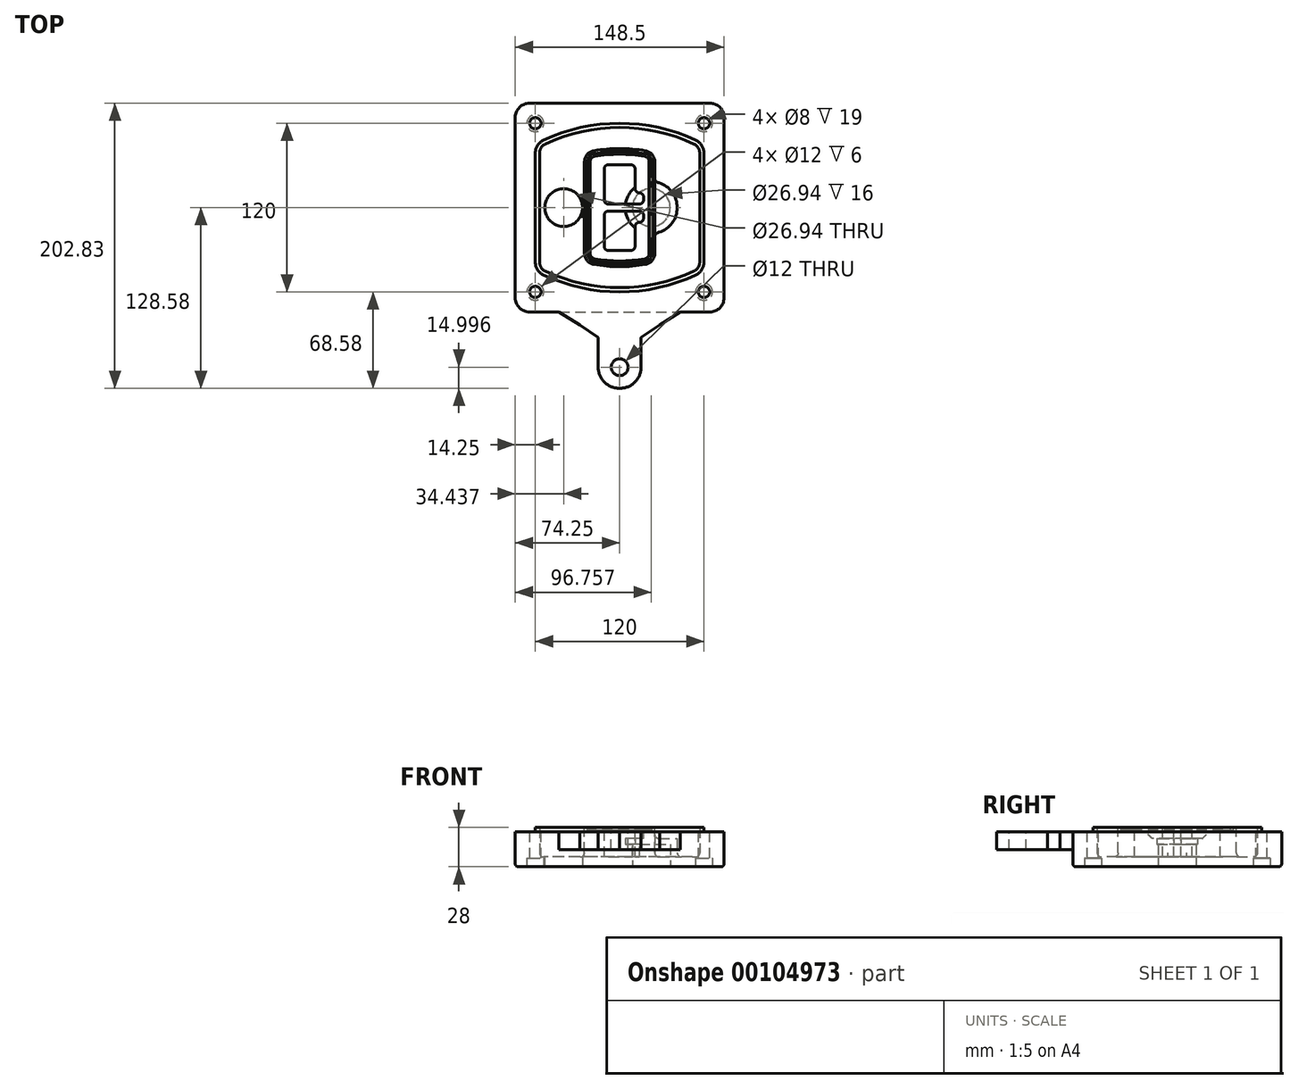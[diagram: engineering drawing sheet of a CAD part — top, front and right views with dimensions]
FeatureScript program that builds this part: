
annotation { "Feature Type Name" : "Feature", "Feature Type Description" : "" }
export const myFeature = defineFeature(function(context is Context, id is Id, definition is map)
    precondition{}
    {
        {
            var Q0;
            Q0=qCreatedBy(makeId("Top.planeOp"),FACE);
            var sketch = newSketch(context, id + "F0", { "sketchPlane" : qUnion([Q0])});
            skPoint(sketch, "E0.rect.middle", {"position": v(0, 0) * mm});
            skLineSegment(sketch, "E1.bottom", {"start": v(-64.25, -74.25) * mm, "end": v(64.25, -74.25) * mm});
            skLineSegment(sketch, "E1.top", {"start": v(-64.25, 74.25) * mm, "end": v(64.25, 74.25) * mm});
            skLineSegment(sketch, "E1.left", {"start": v(-74.25, -64.25) * mm, "end": v(-74.25, 64.25) * mm});
            skLineSegment(sketch, "E1.right", {"start": v(74.25, -64.25) * mm, "end": v(74.25, 64.25) * mm});
            skLineSegment(sketch, "E2", {"start": v(-74.25, 74.25) * mm, "end": v(74.25, -74.25) * mm, "construction": true});
            skLineSegment(sketch, "E3", {"start": v(74.25, 74.25) * mm, "end": v(-74.25, -74.25) * mm, "construction": true});
            skCircle(sketch, "E4", {"center": v(-60, 60) * mm, "radius": 4 * mm});
            skCircle(sketch, "E5", {"center": v(60, 60) * mm, "radius": 4 * mm});
            skCircle(sketch, "E6", {"center": v(60, -60) * mm, "radius": 4 * mm});
            skCircle(sketch, "E7", {"center": v(-60, -60) * mm, "radius": 4 * mm});
            skLineSegment(sketch, "E8", {"start": v(-60, 60) * mm, "end": v(60, 60) * mm, "construction": true});
            skLineSegment(sketch, "E9", {"start": v(60, 60) * mm, "end": v(60, -60) * mm, "construction": true});
            skLineSegment(sketch, "E10", {"start": v(60, -60) * mm, "end": v(-60, -60) * mm, "construction": true});
            skLineSegment(sketch, "E11", {"start": v(-60, -60) * mm, "end": v(-60, 60) * mm, "construction": true});
            skLineSegment(sketch, "E12", {"start": v(-60, 38.83) * mm, "end": v(-60, -38.83) * mm});
            skLineSegment(sketch, "E13", {"start": v(60, 38.83) * mm, "end": v(60, -38.83) * mm});
            skArc(sketch, "E14", {"start": v(54.26, 47.88) * mm, "mid": v(0, 60) * mm, "end": v(-54.26, 47.88) * mm});
            skArc(sketch, "E15", {"start": v(-54.26, -47.88) * mm, "mid": v(0, -60) * mm, "end": v(54.26, -47.88) * mm});
            skLineSegment(sketch, "E16", {"start": v(-60, 0) * mm, "end": v(60, 0) * mm, "construction": true});
            skPoint(sketch, "E17.visualSharp", {"position": v(-60, -45) * mm});
            skArc(sketch, "E17.filletArc", {"start": v(-60, -38.83) * mm, "mid": v(-58.44, -44.2) * mm, "end": v(-54.26, -47.88) * mm});
            skPoint(sketch, "E18.visualSharp", {"position": v(-60, 45) * mm});
            skArc(sketch, "E18.filletArc", {"start": v(-54.26, 47.88) * mm, "mid": v(-58.44, 44.2) * mm, "end": v(-60, 38.83) * mm});
            skPoint(sketch, "E19.visualSharp", {"position": v(60, 45) * mm});
            skArc(sketch, "E19.filletArc", {"start": v(60, 38.83) * mm, "mid": v(58.44, 44.2) * mm, "end": v(54.26, 47.88) * mm});
            skPoint(sketch, "E20.visualSharp", {"position": v(60, -45) * mm});
            skArc(sketch, "E20.filletArc", {"start": v(54.26, -47.88) * mm, "mid": v(58.44, -44.2) * mm, "end": v(60, -38.83) * mm});
            skPoint(sketch, "E21.visualSharp", {"position": v(-74.25, 74.25) * mm});
            skArc(sketch, "E21.filletArc", {"start": v(-64.25, 74.25) * mm, "mid": v(-71.32, 71.32) * mm, "end": v(-74.25, 64.25) * mm});
            skPoint(sketch, "E22.visualSharp", {"position": v(74.25, 74.25) * mm});
            skArc(sketch, "E22.filletArc", {"start": v(74.25, 64.25) * mm, "mid": v(71.32, 71.32) * mm, "end": v(64.25, 74.25) * mm});
            skPoint(sketch, "E23.visualSharp", {"position": v(74.25, -74.25) * mm});
            skArc(sketch, "E23.filletArc", {"start": v(64.25, -74.25) * mm, "mid": v(71.32, -71.32) * mm, "end": v(74.25, -64.25) * mm});
            skPoint(sketch, "E24.visualSharp", {"position": v(-74.25, -74.25) * mm});
            skArc(sketch, "E24.filletArc", {"start": v(-74.25, -64.25) * mm, "mid": v(-71.32, -71.32) * mm, "end": v(-64.25, -74.25) * mm});
            skArc(sketch, "E25.0", {"start": v(57, 38.83) * mm, "mid": v(55.9, 42.58) * mm, "end": v(52.98, 45.17) * mm});
            skLineSegment(sketch, "E25.1", {"start": v(57, 38.83) * mm, "end": v(57, -38.83) * mm});
            skArc(sketch, "E25.2", {"start": v(52.98, -45.17) * mm, "mid": v(55.9, -42.58) * mm, "end": v(57, -38.83) * mm});
            skArc(sketch, "E25.3", {"start": v(-52.98, -45.17) * mm, "mid": v(0, -57) * mm, "end": v(52.98, -45.17) * mm});
            skArc(sketch, "E25.4", {"start": v(-57, -38.83) * mm, "mid": v(-55.9, -42.58) * mm, "end": v(-52.98, -45.17) * mm});
            skArc(sketch, "E25.5", {"start": v(52.98, 45.17) * mm, "mid": v(0, 57) * mm, "end": v(-52.98, 45.17) * mm});
            skLineSegment(sketch, "E25.6", {"start": v(-57, 38.83) * mm, "end": v(-57, -38.83) * mm});
            skArc(sketch, "E25.7", {"start": v(-52.98, 45.17) * mm, "mid": v(-55.9, 42.58) * mm, "end": v(-57, 38.83) * mm});
            skArc(sketch, "E26.0", {"start": v(-55.96, 51.5) * mm, "mid": v(-61.82, 46.33) * mm, "end": v(-64, 38.83) * mm});
            skArc(sketch, "E26.1", {"start": v(55.96, 51.5) * mm, "mid": v(0, 64) * mm, "end": v(-55.96, 51.5) * mm});
            skArc(sketch, "E26.2", {"start": v(64, 38.83) * mm, "mid": v(61.82, 46.33) * mm, "end": v(55.96, 51.5) * mm});
            skLineSegment(sketch, "E26.3", {"start": v(64, 38.83) * mm, "end": v(64, -38.83) * mm});
            skArc(sketch, "E26.4", {"start": v(55.96, -51.5) * mm, "mid": v(61.82, -46.33) * mm, "end": v(64, -38.83) * mm});
            skLineSegment(sketch, "E26.5", {"start": v(-64, 38.83) * mm, "end": v(-64, -38.83) * mm});
            skArc(sketch, "E26.6", {"start": v(-55.96, -51.5) * mm, "mid": v(0, -64) * mm, "end": v(55.96, -51.5) * mm});
            skArc(sketch, "E26.7", {"start": v(-64, -38.83) * mm, "mid": v(-61.82, -46.33) * mm, "end": v(-55.96, -51.5) * mm});
            skSolve(sketch);
        }
        {
            var Q0;
            Q0=makeQuery(id+"F0.imprint","IMPRINT",FACE,{"disambiguationData":[TD([[makeQuery(id+"F0.imprint","IMPRINT",EDGE,{"derivedFrom":sQuery(id+"F0.wireOp",EDGE,"E1.bottom")}),1.0]])]});
            var Q1;
            Q1=makeQuery(id+"F0.imprint","IMPRINT",FACE,{"disambiguationData":[TD([[makeQuery(id+"F0.imprint","IMPRINT",EDGE,{"derivedFrom":sQuery(id+"F0.wireOp",EDGE,"E12")}),1.0]])]});
            var Q2;
            Q2=makeQuery(id+"F0.imprint","IMPRINT",FACE,{"disambiguationData":[TD([[makeQuery(id+"F0.imprint","IMPRINT",EDGE,{"derivedFrom":sQuery(id+"F0.wireOp",EDGE,"E25.0")}),1.0]])]});
            var Q3;
            Q3=makeQuery(id+"F0.imprint","IMPRINT",FACE,{"disambiguationData":[TD([[makeQuery(id+"F0.imprint","IMPRINT",EDGE,{"derivedFrom":sQuery(id+"F0.wireOp",EDGE,"E12")}),-1.0]])]});
            extrude(context, id + "F1", {"entities" : qUnion([Q0, Q1, Q2, Q3]), "oppositeDirection" : true, "depth" : 25 * mm});
        }
        {
            var Q0;
            Q0=makeQuery(id+"F0.imprint","IMPRINT",FACE,{"disambiguationData":[TD([[makeQuery(id+"F0.imprint","IMPRINT",EDGE,{"derivedFrom":sQuery(id+"F0.wireOp",EDGE,"E12")}),1.0]])]});
            extrude(context, id + "F2", {"entities" : qUnion([Q0]), "operationType" : NewBodyOperationType.ADD, "depth" : 3 * mm});
        }
        {
            var Q0;
            Q0=makeQuery(id+"F0.imprint","IMPRINT",FACE,{"disambiguationData":[TD([[makeQuery(id+"F0.imprint","IMPRINT",EDGE,{"derivedFrom":sQuery(id+"F0.wireOp",EDGE,"E25.0")}),1.0]])]});
            extrude(context, id + "F3", {"entities" : qUnion([Q0]), "operationType" : NewBodyOperationType.REMOVE, "oppositeDirection" : true, "depth" : 18 * mm});
        }
        {
            var Q0;
            Q0=makeQuery(id+"F2.opExtrude","CAP_FACE",FACE,{"disambiguationData":[OSD([sQuery(id+"F0.wireOp",EDGE,"E12"),sQuery(id+"F0.wireOp",EDGE,"E13"),sQuery(id+"F0.wireOp",EDGE,"E14"),sQuery(id+"F0.wireOp",EDGE,"E15"),sQuery(id+"F0.wireOp",EDGE,"E17.filletArc"),sQuery(id+"F0.wireOp",EDGE,"E18.filletArc"),sQuery(id+"F0.wireOp",EDGE,"E19.filletArc"),sQuery(id+"F0.wireOp",EDGE,"E20.filletArc"),sQuery(id+"F0.wireOp",EDGE,"E25.0"),sQuery(id+"F0.wireOp",EDGE,"E25.1"),sQuery(id+"F0.wireOp",EDGE,"E25.2"),sQuery(id+"F0.wireOp",EDGE,"E25.3"),sQuery(id+"F0.wireOp",EDGE,"E25.4"),sQuery(id+"F0.wireOp",EDGE,"E25.5"),sQuery(id+"F0.wireOp",EDGE,"E25.6"),sQuery(id+"F0.wireOp",EDGE,"E25.7")])],"isStart":false});
            var sketch = newSketch(context, id + "F4", { "sketchPlane" : qUnion([Q0])});
            skArc(sketch, "E27.0", {"start": v(-18.34, -40.45) * mm, "mid": v(0, -42) * mm, "end": v(18.34, -40.45) * mm});
            skArc(sketch, "E28.0", {"start": v(18.34, 40.45) * mm, "mid": v(0, 42) * mm, "end": v(-18.34, 40.45) * mm});
            skLineSegment(sketch, "E29", {"start": v(-25, 32.57) * mm, "end": v(-25, -32.57) * mm});
            skLineSegment(sketch, "E30", {"start": v(25, 32.57) * mm, "end": v(25, -32.57) * mm});
            skLineSegment(sketch, "E31", {"start": v(-25, 39.1) * mm, "end": v(25, 39.1) * mm, "construction": true});
            skLineSegment(sketch, "E32", {"start": v(-25, -39.1) * mm, "end": v(25, -39.1) * mm, "construction": true});
            skPoint(sketch, "E33.visualSharp", {"position": v(-25, 39.1) * mm});
            skArc(sketch, "E33.filletArc", {"start": v(-18.34, 40.45) * mm, "mid": v(-23.11, 37.73) * mm, "end": v(-25, 32.57) * mm});
            skPoint(sketch, "E34.visualSharp", {"position": v(25, 39.1) * mm});
            skArc(sketch, "E34.filletArc", {"start": v(25, 32.57) * mm, "mid": v(23.11, 37.73) * mm, "end": v(18.34, 40.45) * mm});
            skPoint(sketch, "E35.visualSharp", {"position": v(25, -39.1) * mm});
            skArc(sketch, "E35.filletArc", {"start": v(18.34, -40.45) * mm, "mid": v(23.11, -37.73) * mm, "end": v(25, -32.57) * mm});
            skPoint(sketch, "E36.visualSharp", {"position": v(-25, -39.1) * mm});
            skArc(sketch, "E36.filletArc", {"start": v(-25, -32.57) * mm, "mid": v(-23.11, -37.73) * mm, "end": v(-18.34, -40.45) * mm});
            skArc(sketch, "E37.0", {"start": v(52.98, 45.17) * mm, "mid": v(0, 57) * mm, "end": v(-52.98, 45.17) * mm});
            skArc(sketch, "E37.1", {"start": v(-52.98, 45.17) * mm, "mid": v(-55.9, 42.58) * mm, "end": v(-57, 38.83) * mm});
            skLineSegment(sketch, "E37.2", {"start": v(-57, 38.83) * mm, "end": v(-57, -38.83) * mm});
            skArc(sketch, "E37.3", {"start": v(-57, -38.83) * mm, "mid": v(-55.9, -42.58) * mm, "end": v(-52.98, -45.17) * mm});
            skArc(sketch, "E37.4", {"start": v(-52.98, -45.17) * mm, "mid": v(0, -57) * mm, "end": v(52.98, -45.17) * mm});
            skArc(sketch, "E37.5", {"start": v(52.98, -45.17) * mm, "mid": v(55.9, -42.58) * mm, "end": v(57, -38.83) * mm});
            skLineSegment(sketch, "E37.6", {"start": v(57, 38.83) * mm, "end": v(57, -38.83) * mm});
            skArc(sketch, "E37.7", {"start": v(57, 38.83) * mm, "mid": v(55.9, 42.58) * mm, "end": v(52.98, 45.17) * mm});
            skLineSegment(sketch, "E38.0", {"start": v(23, 32.57) * mm, "end": v(23, -32.57) * mm});
            skArc(sketch, "E38.1", {"start": v(18, -38.48) * mm, "mid": v(21.58, -36.44) * mm, "end": v(23, -32.57) * mm});
            skArc(sketch, "E38.2", {"start": v(-18, -38.48) * mm, "mid": v(0, -40) * mm, "end": v(18, -38.48) * mm});
            skArc(sketch, "E38.3", {"start": v(-23, -32.57) * mm, "mid": v(-21.58, -36.44) * mm, "end": v(-18, -38.48) * mm});
            skLineSegment(sketch, "E38.4", {"start": v(-23, 32.57) * mm, "end": v(-23, -32.57) * mm});
            skArc(sketch, "E38.5", {"start": v(23, 32.57) * mm, "mid": v(21.58, 36.44) * mm, "end": v(18, 38.48) * mm});
            skArc(sketch, "E38.6", {"start": v(-18, 38.48) * mm, "mid": v(-21.58, 36.44) * mm, "end": v(-23, 32.57) * mm});
            skArc(sketch, "E38.7", {"start": v(18, 38.48) * mm, "mid": v(0, 40) * mm, "end": v(-18, 38.48) * mm});
            skArc(sketch, "E39.0", {"start": v(21, 32.57) * mm, "mid": v(20.06, 35.15) * mm, "end": v(17.67, 36.5) * mm});
            skLineSegment(sketch, "E39.1", {"start": v(21, 32.57) * mm, "end": v(21, -32.57) * mm});
            skArc(sketch, "E39.2", {"start": v(17.67, -36.5) * mm, "mid": v(20.06, -35.15) * mm, "end": v(21, -32.57) * mm});
            skArc(sketch, "E39.3", {"start": v(-17.67, -36.5) * mm, "mid": v(0, -38) * mm, "end": v(17.67, -36.5) * mm});
            skArc(sketch, "E39.4", {"start": v(-21, -32.57) * mm, "mid": v(-20.06, -35.15) * mm, "end": v(-17.67, -36.5) * mm});
            skArc(sketch, "E39.5", {"start": v(17.67, 36.5) * mm, "mid": v(0, 38) * mm, "end": v(-17.67, 36.5) * mm});
            skLineSegment(sketch, "E39.6", {"start": v(-21, 32.57) * mm, "end": v(-21, -32.57) * mm});
            skArc(sketch, "E39.7", {"start": v(-17.67, 36.5) * mm, "mid": v(-20.06, 35.15) * mm, "end": v(-21, 32.57) * mm});
            skLineSegment(sketch, "E40", {"start": v(-25, 0) * mm, "end": v(25, 0) * mm, "construction": true});
            skLineSegment(sketch, "E41", {"start": v(-11, 5.5) * mm, "end": v(-11, 27.5) * mm});
            skLineSegment(sketch, "E42", {"start": v(-8, 30.5) * mm, "end": v(8, 30.5) * mm});
            skLineSegment(sketch, "E43", {"start": v(11, 27.5) * mm, "end": v(11, 13.5) * mm});
            skLineSegment(sketch, "E44", {"start": v(14, 10.5) * mm, "end": v(14, 10.5) * mm});
            skLineSegment(sketch, "E45", {"start": v(17, 7.5) * mm, "end": v(17, 5.5) * mm});
            skLineSegment(sketch, "E46", {"start": v(14, 2.5) * mm, "end": v(-8, 2.5) * mm});
            skPoint(sketch, "E47.visualSharp", {"position": v(-11, 30.5) * mm});
            skArc(sketch, "E47.filletArc", {"start": v(-8, 30.5) * mm, "mid": v(-10.12, 29.62) * mm, "end": v(-11, 27.5) * mm});
            skPoint(sketch, "E48.visualSharp", {"position": v(11, 30.5) * mm});
            skArc(sketch, "E48.filletArc", {"start": v(11, 27.5) * mm, "mid": v(10.12, 29.62) * mm, "end": v(8, 30.5) * mm});
            skPoint(sketch, "E49.visualSharp", {"position": v(11, 10.5) * mm});
            skArc(sketch, "E49.filletArc", {"start": v(11, 13.5) * mm, "mid": v(11.88, 11.38) * mm, "end": v(14, 10.5) * mm});
            skPoint(sketch, "E50.visualSharp", {"position": v(17, 10.5) * mm});
            skArc(sketch, "E50.filletArc", {"start": v(17, 7.5) * mm, "mid": v(16.12, 9.62) * mm, "end": v(14, 10.5) * mm});
            skPoint(sketch, "E51.visualSharp", {"position": v(17, 2.5) * mm});
            skArc(sketch, "E51.filletArc", {"start": v(14, 2.5) * mm, "mid": v(16.12, 3.38) * mm, "end": v(17, 5.5) * mm});
            skPoint(sketch, "E52.visualSharp", {"position": v(-11, 2.5) * mm});
            skArc(sketch, "E52.filletArc", {"start": v(-11, 5.5) * mm, "mid": v(-10.12, 3.38) * mm, "end": v(-8, 2.5) * mm});
            skLineSegment(sketch, "E53.0.MirrorCS", {"start": v(14, -2.5) * mm, "end": v(-8, -2.5) * mm});
            skArc(sketch, "E54.0.MirrorCS", {"start": v(-11, -5.5) * mm, "mid": v(-10.12, -3.38) * mm, "end": v(-8, -2.5) * mm});
            skLineSegment(sketch, "E55.0.MirrorCS", {"start": v(-11, -5.5) * mm, "end": v(-11, -27.5) * mm});
            skArc(sketch, "E56.0.MirrorCS", {"start": v(-8, -30.5) * mm, "mid": v(-10.12, -29.62) * mm, "end": v(-11, -27.5) * mm});
            skLineSegment(sketch, "E57.0.MirrorCS", {"start": v(-8, -30.5) * mm, "end": v(8, -30.5) * mm});
            skArc(sketch, "E58.0.MirrorCS", {"start": v(11, -27.5) * mm, "mid": v(10.12, -29.62) * mm, "end": v(8, -30.5) * mm});
            skLineSegment(sketch, "E59.0.MirrorCS", {"start": v(11, -27.5) * mm, "end": v(11, -13.5) * mm});
            skArc(sketch, "E60.0.MirrorCS", {"start": v(11, -13.5) * mm, "mid": v(11.88, -11.38) * mm, "end": v(14, -10.5) * mm});
            skArc(sketch, "E61.0.MirrorCS", {"start": v(17, -7.5) * mm, "mid": v(16.12, -9.62) * mm, "end": v(14, -10.5) * mm});
            skLineSegment(sketch, "E62.0.MirrorCS", {"start": v(17, -7.5) * mm, "end": v(17, -5.5) * mm});
            skArc(sketch, "E63.0.MirrorCS", {"start": v(14, -2.5) * mm, "mid": v(16.12, -3.38) * mm, "end": v(17, -5.5) * mm});
            skSolve(sketch);
        }
        {
            var Q0;
            Q0=makeQuery(id+"F4.imprint","IMPRINT",FACE,{"disambiguationData":[TD([[makeQuery(id+"F4.imprint","IMPRINT",EDGE,{"derivedFrom":sQuery(id+"F4.wireOp",EDGE,"E27.0")}),1.0]])]});
            var Q1;
            Q1=makeQuery(id+"F4.imprint","IMPRINT",FACE,{"disambiguationData":[TD([[makeQuery(id+"F4.imprint","IMPRINT",EDGE,{"derivedFrom":sQuery(id+"F4.wireOp",EDGE,"E38.0")}),-1.0]])]});
            var Q2;
            Q2=makeQuery(id+"F4.imprint","IMPRINT",FACE,{"disambiguationData":[TD([[makeQuery(id+"F4.imprint","IMPRINT",EDGE,{"derivedFrom":sQuery(id+"F4.wireOp",EDGE,"E39.0")}),1.0]])]});
            extrude(context, id + "F5", {"entities" : qUnion([Q0, Q1, Q2]), "operationType" : NewBodyOperationType.ADD, "endBound" : BoundingType.UP_TO_NEXT, "oppositeDirection" : true, "depth" : 25 * mm});
        }
        {
            var Q0;
            Q0=makeQuery(id+"F4.imprint","IMPRINT",FACE,{"disambiguationData":[TD([[makeQuery(id+"F4.imprint","IMPRINT",EDGE,{"derivedFrom":sQuery(id+"F4.wireOp",EDGE,"E38.0")}),-1.0]])]});
            extrude(context, id + "F6", {"entities" : qUnion([Q0]), "operationType" : NewBodyOperationType.REMOVE, "oppositeDirection" : true, "depth" : 2 * mm});
        }
        {
            var Q0;
            Q0=makeQuery(id+"F1.opExtrude","CAP_FACE",FACE,{"disambiguationData":[OSD([sQuery(id+"F0.wireOp",EDGE,"E1.bottom"),sQuery(id+"F0.wireOp",EDGE,"E1.top"),sQuery(id+"F0.wireOp",EDGE,"E1.left"),sQuery(id+"F0.wireOp",EDGE,"E1.right"),sQuery(id+"F0.wireOp",EDGE,"E4"),sQuery(id+"F0.wireOp",EDGE,"E5"),sQuery(id+"F0.wireOp",EDGE,"E6"),sQuery(id+"F0.wireOp",EDGE,"E7"),sQuery(id+"F0.wireOp",EDGE,"E21.filletArc"),sQuery(id+"F0.wireOp",EDGE,"E22.filletArc"),sQuery(id+"F0.wireOp",EDGE,"E23.filletArc"),sQuery(id+"F0.wireOp",EDGE,"E24.filletArc")])],"isStart":false});
            var sketch = newSketch(context, id + "F7", { "sketchPlane" : qUnion([Q0])});
            skCircle(sketch, "E64", {"center": v(22.5, 0) * mm, "radius": 13.47 * mm});
            skCircle(sketch, "E65", {"center": v(-39.81, 0) * mm, "radius": 13.47 * mm});
            skLineSegment(sketch, "E66", {"start": v(74.25, 0) * mm, "end": v(-74.25, 0) * mm});
            skCircle(sketch, "E67", {"center": v(22.5, 0) * mm, "radius": 18.47 * mm});
            skCircle(sketch, "E68", {"center": v(60, -60) * mm, "radius": 6 * mm});
            skCircle(sketch, "E69", {"center": v(-60, -60) * mm, "radius": 6 * mm});
            skCircle(sketch, "E70", {"center": v(-60, 60) * mm, "radius": 6 * mm});
            skCircle(sketch, "E71", {"center": v(60, 60) * mm, "radius": 6 * mm});
            skSolve(sketch);
        }
        {
            var Q0;
            {var subQ1=sQuery(id+"F7.wireOp",EDGE,"E66");var subQ4=sQuery(id+"F7.wireOp",EDGE,"E64");var subQ6=makeQuery(id+"F7.imprint","INTERSECT",VERTEX,{"disambiguationData":[OD(0.0)],"derivedFrom":[subQ4,subQ1]});Q0=makeQuery(id+"F7.imprint","IMPRINT",FACE,{"disambiguationData":[TD([[makeQuery(id+"F7.imprint","IMPRINT",EDGE,{"disambiguationData":[TD([[subQ6,-1.0]])],"derivedFrom":subQ4}),-1.0]])]});}
            var Q1;
            {var subQ0=sQuery(id+"F7.wireOp",EDGE,"E66");var subQ1=sQuery(id+"F7.wireOp",EDGE,"E64");var subQ3=makeQuery(id+"F7.imprint","INTERSECT",VERTEX,{"disambiguationData":[OD(0.0)],"derivedFrom":[subQ1,subQ0]});Q1=makeQuery(id+"F7.imprint","IMPRINT",FACE,{"disambiguationData":[TD([[makeQuery(id+"F7.imprint","IMPRINT",EDGE,{"disambiguationData":[TD([[subQ3,-1.0]])],"derivedFrom":subQ1}),1.0]])]});}
            var Q2;
            {var subQ0=sQuery(id+"F7.wireOp",EDGE,"E66");var subQ1=sQuery(id+"F7.wireOp",EDGE,"E64");var subQ3=makeQuery(id+"F7.imprint","INTERSECT",VERTEX,{"disambiguationData":[OD(0.0)],"derivedFrom":[subQ1,subQ0]});Q2=makeQuery(id+"F7.imprint","IMPRINT",FACE,{"disambiguationData":[TD([[makeQuery(id+"F7.imprint","IMPRINT",EDGE,{"disambiguationData":[TD([[subQ3,1.0]])],"derivedFrom":subQ1}),1.0]])]});}
            var Q3;
            {var subQ1=sQuery(id+"F7.wireOp",EDGE,"E66");var subQ4=sQuery(id+"F7.wireOp",EDGE,"E64");var subQ6=makeQuery(id+"F7.imprint","INTERSECT",VERTEX,{"disambiguationData":[OD(0.0)],"derivedFrom":[subQ4,subQ1]});Q3=makeQuery(id+"F7.imprint","IMPRINT",FACE,{"disambiguationData":[TD([[makeQuery(id+"F7.imprint","IMPRINT",EDGE,{"disambiguationData":[TD([[subQ6,1.0]])],"derivedFrom":subQ4}),-1.0]])]});}
            extrude(context, id + "F8", {"entities" : qUnion([Q0, Q1, Q2, Q3]), "operationType" : NewBodyOperationType.ADD, "oppositeDirection" : true, "depth" : 20 * mm});
        }
        {
            var Q0;
            {var subQ0=sQuery(id+"F7.wireOp",EDGE,"E66");var subQ1=sQuery(id+"F7.wireOp",EDGE,"E64");var subQ3=makeQuery(id+"F7.imprint","INTERSECT",VERTEX,{"disambiguationData":[OD(0.0)],"derivedFrom":[subQ1,subQ0]});Q0=makeQuery(id+"F7.imprint","IMPRINT",FACE,{"disambiguationData":[TD([[makeQuery(id+"F7.imprint","IMPRINT",EDGE,{"disambiguationData":[TD([[subQ3,-1.0]])],"derivedFrom":subQ1}),1.0]])]});}
            var Q1;
            {var subQ0=sQuery(id+"F7.wireOp",EDGE,"E66");var subQ1=sQuery(id+"F7.wireOp",EDGE,"E64");var subQ3=makeQuery(id+"F7.imprint","INTERSECT",VERTEX,{"disambiguationData":[OD(0.0)],"derivedFrom":[subQ1,subQ0]});Q1=makeQuery(id+"F7.imprint","IMPRINT",FACE,{"disambiguationData":[TD([[makeQuery(id+"F7.imprint","IMPRINT",EDGE,{"disambiguationData":[TD([[subQ3,1.0]])],"derivedFrom":subQ1}),1.0]])]});}
            extrude(context, id + "F9", {"entities" : qUnion([Q0, Q1]), "operationType" : NewBodyOperationType.REMOVE, "oppositeDirection" : true, "depth" : 16 * mm});
        }
        {
            var Q0;
            {var subQ0=sQuery(id+"F7.wireOp",EDGE,"E66");var subQ1=sQuery(id+"F7.wireOp",EDGE,"E65");var subQ3=makeQuery(id+"F7.imprint","INTERSECT",VERTEX,{"disambiguationData":[OD(0.0)],"derivedFrom":[subQ1,subQ0]});Q0=makeQuery(id+"F7.imprint","IMPRINT",FACE,{"disambiguationData":[TD([[makeQuery(id+"F7.imprint","IMPRINT",EDGE,{"disambiguationData":[TD([[subQ3,-1.0]])],"derivedFrom":subQ1}),1.0]])]});}
            var Q1;
            {var subQ0=sQuery(id+"F7.wireOp",EDGE,"E66");var subQ1=sQuery(id+"F7.wireOp",EDGE,"E65");var subQ3=makeQuery(id+"F7.imprint","INTERSECT",VERTEX,{"disambiguationData":[OD(0.0)],"derivedFrom":[subQ1,subQ0]});Q1=makeQuery(id+"F7.imprint","IMPRINT",FACE,{"disambiguationData":[TD([[makeQuery(id+"F7.imprint","IMPRINT",EDGE,{"disambiguationData":[TD([[subQ3,1.0]])],"derivedFrom":subQ1}),1.0]])]});}
            extrude(context, id + "F10", {"entities" : qUnion([Q0, Q1]), "operationType" : NewBodyOperationType.REMOVE, "oppositeDirection" : true, "depth" : 25 * mm});
        }
        {
            var Q0;
            Q0=makeQuery(id+"F7.imprint","IMPRINT",FACE,{"disambiguationData":[TD([[makeQuery(id+"F7.imprint","IMPRINT",EDGE,{"derivedFrom":sQuery(id+"F7.wireOp",EDGE,"E68")}),1.0]])]});
            var Q1;
            Q1=makeQuery(id+"F7.imprint","IMPRINT",FACE,{"disambiguationData":[TD([[makeQuery(id+"F7.imprint","IMPRINT",EDGE,{"derivedFrom":makeQuery(id+"F1.opExtrude","CAP_EDGE",EDGE,{"disambiguationData":[OSD([sQuery(id+"F0.wireOp",EDGE,"E5")])],"isStart":false})}),-1.0]])]});
            var Q2;
            Q2=makeQuery(id+"F7.imprint","IMPRINT",FACE,{"disambiguationData":[TD([[makeQuery(id+"F7.imprint","IMPRINT",EDGE,{"derivedFrom":sQuery(id+"F7.wireOp",EDGE,"E69")}),1.0]])]});
            var Q3;
            Q3=makeQuery(id+"F7.imprint","IMPRINT",FACE,{"disambiguationData":[TD([[makeQuery(id+"F7.imprint","IMPRINT",EDGE,{"derivedFrom":makeQuery(id+"F1.opExtrude","CAP_EDGE",EDGE,{"disambiguationData":[OSD([sQuery(id+"F0.wireOp",EDGE,"E4")])],"isStart":false})}),-1.0]])]});
            var Q4;
            Q4=makeQuery(id+"F7.imprint","IMPRINT",FACE,{"disambiguationData":[TD([[makeQuery(id+"F7.imprint","IMPRINT",EDGE,{"derivedFrom":sQuery(id+"F7.wireOp",EDGE,"E70")}),1.0]])]});
            var Q5;
            Q5=makeQuery(id+"F7.imprint","IMPRINT",FACE,{"disambiguationData":[TD([[makeQuery(id+"F7.imprint","IMPRINT",EDGE,{"derivedFrom":makeQuery(id+"F1.opExtrude","CAP_EDGE",EDGE,{"disambiguationData":[OSD([sQuery(id+"F0.wireOp",EDGE,"E7")])],"isStart":false})}),-1.0]])]});
            var Q6;
            Q6=makeQuery(id+"F7.imprint","IMPRINT",FACE,{"disambiguationData":[TD([[makeQuery(id+"F7.imprint","IMPRINT",EDGE,{"derivedFrom":sQuery(id+"F7.wireOp",EDGE,"E71")}),1.0]])]});
            var Q7;
            Q7=makeQuery(id+"F7.imprint","IMPRINT",FACE,{"disambiguationData":[TD([[makeQuery(id+"F7.imprint","IMPRINT",EDGE,{"derivedFrom":makeQuery(id+"F1.opExtrude","CAP_EDGE",EDGE,{"disambiguationData":[OSD([sQuery(id+"F0.wireOp",EDGE,"E6")])],"isStart":false})}),-1.0]])]});
            extrude(context, id + "F11", {"entities" : qUnion([Q0, Q1, Q2, Q3, Q4, Q5, Q6, Q7]), "operationType" : NewBodyOperationType.REMOVE, "oppositeDirection" : true, "depth" : 6 * mm});
        }
        {
            var Q0;
            Q0=makeQuery(id+"F9.boolean.opBoolean","COPY",FACE,{"derivedFrom":makeQuery(id+"F9.opExtrude","CAP_FACE",FACE,{"disambiguationData":[OSD([sQuery(id+"F7.wireOp",EDGE,"E64")])],"isStart":false})});
            var sketch = newSketch(context, id + "F12", { "sketchPlane" : qUnion([Q0])});
            skArc(sketch, "E72.0", {"start": v(11, 14.45) * mm, "mid": v(6.45, 9.13) * mm, "end": v(4.2, 2.5) * mm});
            skArc(sketch, "E72.1", {"start": v(4.2, -2.5) * mm, "mid": v(6.45, -9.13) * mm, "end": v(11, -14.45) * mm});
            skLineSegment(sketch, "E73", {"start": v(4.2, -2.5) * mm, "end": v(14, -2.5) * mm});
            skLineSegment(sketch, "E74.0", {"start": v(14, 2.5) * mm, "end": v(4.2, 2.5) * mm});
            skArc(sketch, "E74.1", {"start": v(14, 2.5) * mm, "mid": v(16.12, 3.38) * mm, "end": v(17, 5.5) * mm});
            skLineSegment(sketch, "E74.2", {"start": v(17, 7.5) * mm, "end": v(17, 5.5) * mm});
            skArc(sketch, "E74.3", {"start": v(17, 7.5) * mm, "mid": v(16.12, 9.62) * mm, "end": v(14, 10.5) * mm});
            skArc(sketch, "E74.4", {"start": v(11, 13.5) * mm, "mid": v(11.88, 11.38) * mm, "end": v(14, 10.5) * mm});
            skLineSegment(sketch, "E74.5", {"start": v(11, 14.45) * mm, "end": v(11, 13.5) * mm});
            skLineSegment(sketch, "E74.7", {"start": v(14, -2.5) * mm, "end": v(4.2, -2.5) * mm});
            skArc(sketch, "E74.8", {"start": v(14, -2.5) * mm, "mid": v(16.12, -3.38) * mm, "end": v(17, -5.5) * mm});
            skLineSegment(sketch, "E74.9", {"start": v(17, -7.5) * mm, "end": v(17, -5.5) * mm});
            skArc(sketch, "E74.10", {"start": v(17, -7.5) * mm, "mid": v(16.12, -9.62) * mm, "end": v(14, -10.5) * mm});
            skArc(sketch, "E74.11", {"start": v(11, -13.5) * mm, "mid": v(11.88, -11.38) * mm, "end": v(14, -10.5) * mm});
            skLineSegment(sketch, "E74.12", {"start": v(11, -14.45) * mm, "end": v(11, -13.5) * mm});
            skPoint(sketch, "E75.orphan", {"position": v(11, -27.5) * mm});
            skPoint(sketch, "E76.orphan", {"position": v(-8, -2.5) * mm});
            skPoint(sketch, "E77.orphan", {"position": v(-8, 2.5) * mm});
            skPoint(sketch, "E78.orphan", {"position": v(11, 27.5) * mm});
            skSolve(sketch);
        }
        {
            var Q0;
            {var subQ7=sQuery(id+"F12.wireOp",EDGE,"E72.0");var subQ14=sQuery(id+"F12.wireOp",EDGE,"E72.1");var subQ16=sQuery(id+"F12.wireOp",EDGE,"E74.1");var subQ18=sQuery(id+"F12.wireOp",EDGE,"E74.8");Q0=qUnion([makeQuery(id+"F12.imprint","IMPRINT",FACE,{"disambiguationData":[TD([[makeQuery(id+"F12.imprint","IMPRINT",EDGE,{"derivedFrom":subQ7}),1.0]])]}),makeQuery(id+"F12.imprint","IMPRINT",FACE,{"disambiguationData":[TD([[makeQuery(id+"F12.imprint","IMPRINT",EDGE,{"derivedFrom":subQ14}),1.0]])]}),makeQuery(id+"F12.imprint","IMPRINT",FACE,{"disambiguationData":[TD([[makeQuery(id+"F12.imprint","IMPRINT",EDGE,{"derivedFrom":subQ16}),1.0]])]}),makeQuery(id+"F12.imprint","IMPRINT",FACE,{"disambiguationData":[TD([[makeQuery(id+"F12.imprint","IMPRINT",EDGE,{"derivedFrom":subQ18}),-1.0]])]})]);}
            var Q1;
            Q1=makeQuery(id+"F5.boolean.opBoolean","SPLIT",FACE,{"disambiguationData":[TD([makeQuery(id+"F5.opExtrude","SWEPT_FACE",FACE,{"disambiguationData":[OSD([sQuery(id+"F4.wireOp",EDGE,"E41")])]})])],"derivedFrom":makeQuery(id+"F3.boolean.opBoolean","COPY",FACE,{"derivedFrom":makeQuery(id+"F3.opExtrude","CAP_FACE",FACE,{"disambiguationData":[OSD([sQuery(id+"F0.wireOp",EDGE,"E25.0"),sQuery(id+"F0.wireOp",EDGE,"E25.1"),sQuery(id+"F0.wireOp",EDGE,"E25.2"),sQuery(id+"F0.wireOp",EDGE,"E25.3"),sQuery(id+"F0.wireOp",EDGE,"E25.4"),sQuery(id+"F0.wireOp",EDGE,"E25.5"),sQuery(id+"F0.wireOp",EDGE,"E25.6"),sQuery(id+"F0.wireOp",EDGE,"E25.7")])],"isStart":false})})});
            extrude(context, id + "F13", {"entities" : qUnion([Q0]), "operationType" : NewBodyOperationType.REMOVE, "endBound" : BoundingType.UP_TO_SURFACE, "endBoundEntityFace" : qUnion([Q1]), "depth" : 25 * mm});
        }
        {
            var Q0;
            Q0=makeQuery(id+"F3.boolean.opBoolean","COPY",EDGE,{"derivedFrom":makeQuery(id+"F3.opExtrude","CAP_EDGE",EDGE,{"disambiguationData":[OSD([sQuery(id+"F0.wireOp",EDGE,"E25.6")])],"isStart":false})});
            var Q1;
            Q1=makeQuery(id+"F8.boolean.opBoolean","INTERSECT",EDGE,{"derivedFrom":[makeQuery(id+"F5.opExtrude","SWEPT_FACE",FACE,{"disambiguationData":[OSD([sQuery(id+"F4.wireOp",EDGE,"E30")])]}),makeQuery(id+"F8.opExtrude","CAP_FACE",FACE,{"disambiguationData":[OSD([sQuery(id+"F7.wireOp",EDGE,"E67")])],"isStart":false})]});
            var Q2;
            Q2=makeQuery(id+"F8.boolean.opBoolean","INTERSECT",EDGE,{"disambiguationData":[OD(1.0)],"derivedFrom":[makeQuery(id+"F5.opExtrude","SWEPT_FACE",FACE,{"disambiguationData":[OSD([sQuery(id+"F4.wireOp",EDGE,"E30")])]}),makeQuery(id+"F8.opExtrude","SWEPT_FACE",FACE,{"disambiguationData":[OSD([sQuery(id+"F7.wireOp",EDGE,"E67")])]})]});
            var Q3;
            {var subQ0=sQuery(id+"F4.wireOp",EDGE,"E30");Q3=makeQuery(id+"F8.boolean.opBoolean","SPLIT",EDGE,{"disambiguationData":[TD([makeQuery(id+"F5.opExtrude","SWEPT_FACE",FACE,{"disambiguationData":[OSD([sQuery(id+"F4.wireOp",EDGE,"E35.filletArc")])]})])],"derivedFrom":makeQuery(id+"F5.opExtrude","CAP_EDGE",EDGE,{"disambiguationData":[OSD([subQ0])],"isStart":false})});}
            var Q4;
            {var subQ0=sQuery(id+"F0.wireOp",EDGE,"E25.7");var subQ1=sQuery(id+"F0.wireOp",EDGE,"E25.1");var subQ2=sQuery(id+"F0.wireOp",EDGE,"E25.6");var subQ3=sQuery(id+"F0.wireOp",EDGE,"E25.5");var subQ4=sQuery(id+"F0.wireOp",EDGE,"E25.4");var subQ5=sQuery(id+"F0.wireOp",EDGE,"E25.0");var subQ6=sQuery(id+"F0.wireOp",EDGE,"E25.2");var subQ7=sQuery(id+"F0.wireOp",EDGE,"E25.3");Q4=makeQuery(id+"F8.boolean.opBoolean","INTERSECT",EDGE,{"derivedFrom":[makeQuery(id+"F5.boolean.opBoolean","SPLIT",FACE,{"disambiguationData":[TD([makeQuery(id+"F2.opExtrude","SWEPT_FACE",FACE,{"disambiguationData":[OSD([subQ5])]})])],"derivedFrom":makeQuery(id+"F3.boolean.opBoolean","COPY",FACE,{"derivedFrom":makeQuery(id+"F3.opExtrude","CAP_FACE",FACE,{"disambiguationData":[OSD([subQ5,subQ1,subQ6,subQ7,subQ4,subQ3,subQ2,subQ0])],"isStart":false})})}),makeQuery(id+"F8.opExtrude","SWEPT_FACE",FACE,{"disambiguationData":[OSD([sQuery(id+"F7.wireOp",EDGE,"E67")])]})]});}
            var Q5;
            Q5=makeQuery(id+"F8.boolean.opBoolean","INTERSECT",EDGE,{"disambiguationData":[OD(0.0)],"derivedFrom":[makeQuery(id+"F5.opExtrude","SWEPT_FACE",FACE,{"disambiguationData":[OSD([sQuery(id+"F4.wireOp",EDGE,"E30")])]}),makeQuery(id+"F8.opExtrude","SWEPT_FACE",FACE,{"disambiguationData":[OSD([sQuery(id+"F7.wireOp",EDGE,"E67")])]})]});
            fillet(context, id + "F14", {"entities" : qUnion([Q0, Q1, Q2, Q3, Q4, Q5]), "radius" : 3 * mm, "tangentPropagation" : true, "allowEdgeOverflow" : false});
        }
        {
            var Q0;
            Q0=makeQuery(id+"F1.opExtrude","CAP_EDGE",EDGE,{"disambiguationData":[OSD([sQuery(id+"F0.wireOp",EDGE,"E1.bottom")])],"isStart":false});
            fillet(context, id + "F15", {"entities" : qUnion([Q0]), "radius" : 2 * mm, "tangentPropagation" : true, "allowEdgeOverflow" : false});
        }
        {
            var Q0;
            {var subQ0=sQuery(id+"F0.wireOp",EDGE,"E22.filletArc");var subQ1=sQuery(id+"F0.wireOp",EDGE,"E7");var subQ2=sQuery(id+"F0.wireOp",EDGE,"E6");var subQ3=sQuery(id+"F0.wireOp",EDGE,"E5");var subQ4=sQuery(id+"F0.wireOp",EDGE,"E4");var subQ5=sQuery(id+"F0.wireOp",EDGE,"E1.bottom");var subQ6=sQuery(id+"F0.wireOp",EDGE,"E21.filletArc");var subQ7=sQuery(id+"F0.wireOp",EDGE,"E1.top");var subQ8=sQuery(id+"F0.wireOp",EDGE,"E1.left");var subQ9=sQuery(id+"F0.wireOp",EDGE,"E1.right");var subQ10=sQuery(id+"F0.wireOp",EDGE,"E23.filletArc");var subQ11=sQuery(id+"F0.wireOp",EDGE,"E24.filletArc");Q0=makeQuery(id+"F2.boolean.opBoolean","SPLIT",FACE,{"disambiguationData":[TD([makeQuery(id+"F1.opExtrude","SWEPT_FACE",FACE,{"disambiguationData":[OSD([subQ5])]})])],"derivedFrom":makeQuery(id+"F1.opExtrude","CAP_FACE",FACE,{"disambiguationData":[OSD([subQ5,subQ7,subQ8,subQ9,subQ4,subQ3,subQ2,subQ1,subQ6,subQ0,subQ10,subQ11])],"isStart":true})});}
            var sketch = newSketch(context, id + "F16", { "sketchPlane" : qUnion([Q0])});
            skSolve(sketch);
        }
        {
            var Q0;
            Q0=makeQuery(id+"F16.imprint","IMPRINT",FACE,{"disambiguationData":[TD([[makeQuery(id+"F16.imprint","IMPRINT",EDGE,{"derivedFrom":makeQuery(id+"F1.opExtrude","CAP_EDGE",EDGE,{"disambiguationData":[OSD([sQuery(id+"F0.wireOp",EDGE,"E1.bottom")])],"isStart":true})}),1.0]])]});
            var sketch = newSketch(context, id + "F17", { "sketchPlane" : qUnion([Q0])});
            skLineSegment(sketch, "E79", {"start": v(0, -74.36) * mm, "end": v(0, -113.58) * mm, "construction": true});
            skCircle(sketch, "E80", {"center": v(0, -113.58) * mm, "radius": 6 * mm});
            skLineSegment(sketch, "E81", {"start": v(28.4, -83.58) * mm, "end": v(15.27, -92.25) * mm});
            skLineSegment(sketch, "E82", {"start": v(15.27, -92.25) * mm, "end": v(15.27, -113.58) * mm});
            skLineSegment(sketch, "E83", {"start": v(-26.96, -83.58) * mm, "end": v(-14.73, -92.25) * mm});
            skLineSegment(sketch, "E84", {"start": v(-14.73, -92.25) * mm, "end": v(-14.73, -113.58) * mm});
            skArc(sketch, "E85", {"start": v(-14.73, -113.58) * mm, "mid": v(0.27, -128.58) * mm, "end": v(15.27, -113.58) * mm});
            skLineSegment(sketch, "E86", {"start": v(28.4, -83.58) * mm, "end": v(43.16, -74.21) * mm});
            skLineSegment(sketch, "E87", {"start": v(-26.96, -83.58) * mm, "end": v(-40.2, -74.34) * mm});
            skLineSegment(sketch, "E88", {"start": v(74.96, 0) * mm, "end": v(-73.98, 0) * mm, "construction": true});
            skLineSegment(sketch, "E89.MirrorCS", {"start": v(-28.4, -83.58) * mm, "end": v(-15.27, -92.25) * mm});
            skLineSegment(sketch, "E90.MirrorCS", {"start": v(-15.27, -92.25) * mm, "end": v(-15.27, -113.58) * mm});
            skLineSegment(sketch, "E91.MirrorCS", {"start": v(14.73, -92.25) * mm, "end": v(14.73, -113.58) * mm});
            skArc(sketch, "E92.MirrorCS", {"start": v(14.73, -113.58) * mm, "mid": v(-0.27, -128.58) * mm, "end": v(-15.27, -113.58) * mm});
            skLineSegment(sketch, "E93.MirrorCS", {"start": v(26.96, -83.58) * mm, "end": v(14.73, -92.25) * mm});
            skLineSegment(sketch, "E94.MirrorCS", {"start": v(-28.4, -83.58) * mm, "end": v(-43.16, -74.21) * mm});
            skLineSegment(sketch, "E95.MirrorCS", {"start": v(26.96, -83.58) * mm, "end": v(40.2, -74.34) * mm});
            skSolve(sketch);
        }
        {
            var Q0;
            {var subQ1=sQuery(id+"F17.wireOp",EDGE,"E81");Q0=makeQuery(id+"F17.imprint","IMPRINT",FACE,{"disambiguationData":[TD([[makeQuery(id+"F17.imprint","IMPRINT",EDGE,{"derivedFrom":subQ1}),-1.0]])]});}
            var sketch = newSketch(context, id + "F18", { "sketchPlane" : qUnion([Q0])});
            skSolve(sketch);
        }
        {
            var Q0;
            Q0 = qSketchRegion(id + "F18", true);
            var Q1;
            {var subQ1=sQuery(id+"F17.wireOp",EDGE,"E81");Q1=makeQuery(id+"F17.imprint","IMPRINT",FACE,{"disambiguationData":[TD([[makeQuery(id+"F17.imprint","IMPRINT",EDGE,{"derivedFrom":subQ1}),-1.0]])]});}
            extrude(context, id + "F19", {"entities" : qUnion([Q0, Q1]), "operationType" : NewBodyOperationType.ADD, "oppositeDirection" : true, "depth" : 12.88 * mm});
        }
    });
